# Revit family: Haworth_Planes_ConferenceTable_RoundOnePiece
name_source: partatom
category: Furniture Systems
revit_build: Autodesk Revit 2018 (Build: 20170223_1515(x64)
units: mm (PartAtom-declared; Revit-internal decimal feet)

## family parameters
Always vertical = Yes
Cut with Voids When Loaded = No
OmniClass Number = 23.40.70.14.64.21
OmniClass Title = Systems Furniture
Part Type = Normal
Room Calculation Point = No
Round Connector Dimension = Use Diameter
Shared = No
Work Plane-Based = No

## types (4) — shared parameters
Actual Height = 29"
Assembly Code = E2020200
Cable Base = Yes
Cable Base 14x14 = Yes
Custom Size = No
Cutout = No
Description = Haworth - Planes - Conference - Table Round - One Piece
Edgeband = Yes
Flip Top = No
Flip Top Finish = Haworth _ Paint _ Metallic Champagne
Knife Edge = No
Leg Height = 27 13/16"
Manufacturer = Haworth
Max Diameter = 72"
Min Diameter = 42"
Min/Max Diameter = 42-72 in. @ 6 in. increments
Model = TARN
Opening Double = No
Opening Double Wide = No
Opening Single = No
Opening Single Wide = No
Revision Number = 4
Size = Verify Final Dim. w/ Haworth
Support Post Standard = Yes
Sustainability Info = http://www.haworth.com
Table Thickness = 1 3/16"
URL = www.haworth.com
URL - Product = http://www.haworth.com
Warranty = http://www.haworth.com

## per-type parameters (varying)
| type | Actual Diameter | Diameter | Radius | Support Spacing - From Edge |
| 42dia | 42" | 42" | 21" | 17 13/16" |
| 48dia | 48" | 48" | 24" | 20 13/16" |
| 54dia | 54" | 54" | 27" | 23 13/16" |
| 60dia | 60" | 60" | 30" | 26 13/16" |

## geometry (parser evidence)
native form markers: Sweep x8
no freeform markers — native parametric forms only
